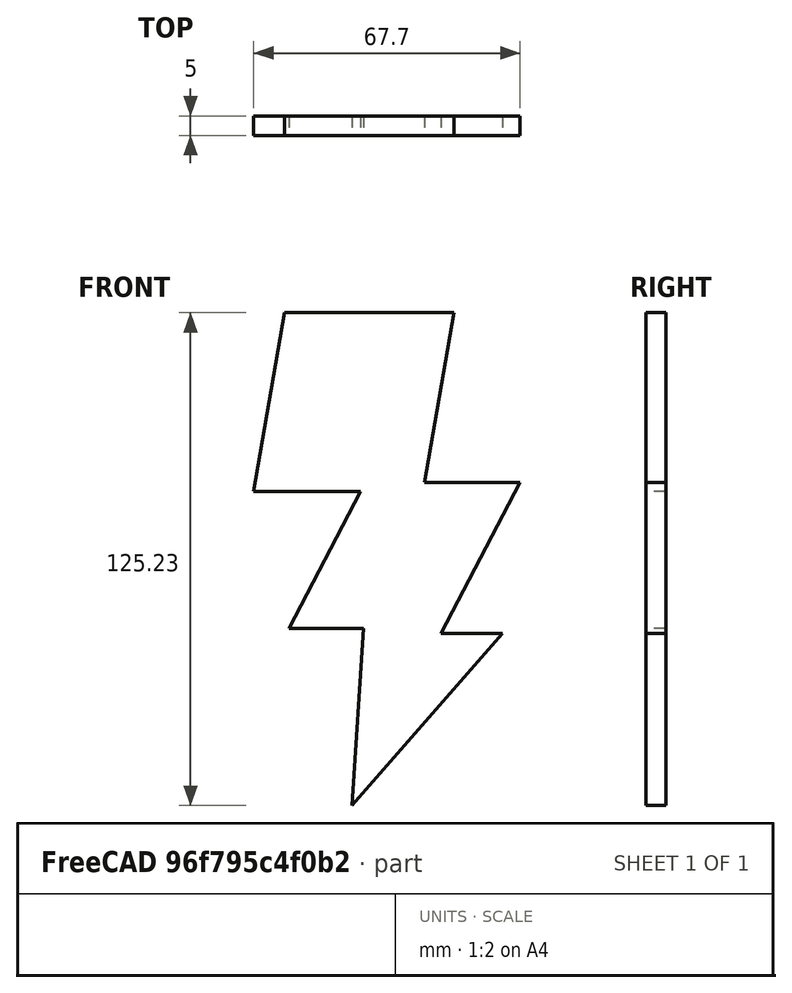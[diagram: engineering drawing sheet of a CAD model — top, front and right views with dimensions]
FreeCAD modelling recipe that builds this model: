
FCSTD DOCUMENT  (FreeCAD 0.18R16146 (Git))
Label: rayo
License: All rights reserved
LicenseURL: http://en.wikipedia.org/wiki/All_rights_reserved
objects: Sketcher::SketchObject×1, PartDesign::Pad×1, PartDesign::Body×1
note: 4 computed .brp shape members not serialized (recipe doc carries the construction recipe); baked Part::Feature solids carry a one-line shape summary decoded from their .brp

FEATURE [Sketcher::SketchObject] Sketch
  MapMode = 5
  Placement = pos=(0,0,0) rot=(1,0,0;1.5708rad)
  Support = -> [XZ_Plane]
  sketch-geometry (11):
    g0: LineSegment StartX=16.8096 StartY=52.0515 StartZ=0 EndX=59.8494 EndY=52.0515 EndZ=0
    g1: LineSegment StartX=59.8494 StartY=52.0515 StartZ=0 EndX=52.4519 EndY=8.97812 EndZ=0
    g2: LineSegment StartX=52.4519 StartY=8.97812 StartZ=0 EndX=76.7074 EndY=8.97812 EndZ=0
    g3: LineSegment StartX=76.7074 StartY=8.97812 StartZ=0 EndX=56.5991 EndY=-29.4804 EndZ=0
    g4: LineSegment StartX=56.5991 StartY=-29.4804 StartZ=0 EndX=72.2487 EndY=-29.4804 EndZ=0
    g5: LineSegment StartX=72.2487 StartY=-29.4804 StartZ=0 EndX=34.0234 EndY=-73.1768 EndZ=0
    g6: LineSegment StartX=34.0234 StartY=-73.1768 StartZ=0 EndX=36.9265 EndY=-28.1238 EndZ=0
    g7: LineSegment StartX=36.9265 StartY=-28.1238 StartZ=0 EndX=17.9519 EndY=-28.1238 EndZ=0
    g8: LineSegment StartX=17.9519 StartY=-28.1238 StartZ=0 EndX=36.135 EndY=6.65246 EndZ=0
    g9: LineSegment StartX=36.135 StartY=6.65246 StartZ=0 EndX=9.01269 EndY=6.65246 EndZ=0
    g10: LineSegment StartX=9.01269 StartY=6.65246 StartZ=0 EndX=16.8096 EndY=52.0515 EndZ=0
  constraints (18):
    c: Horizontal(g0)
    c: Coincident(g0,g1)
    c: Coincident(g1,g2)
    c: Horizontal(g2)
    c: Coincident(g2,g3)
    c: Coincident(g3,g4)
    c: Horizontal(g4)
    c: Coincident(g4,g5)
    c: Coincident(g5,g6)
    c: Coincident(g6,g7)
    c: Horizontal(g7)
    c: Coincident(g7,g8)
    c: Coincident(g8,g9)
    c: Horizontal(g9)
    c: Coincident(g9,g10)
    c: Coincident(g10,g0)
    c: Parallel(g10,g1)
    c: Parallel(g8,g3)
FEATURE [PartDesign::Pad] Pad
  Length = 5
  Length2 = 100
  Placement = pos=(0,0,0) rot=(1,0,0;1.5708rad)
  Profile = -> Sketch
  Refine = true
  Type = 0
FEATURE [PartDesign::Body] Body
  Group = -> [Sketch,Pad]
  Origin = -> Origin
  Tip = -> Pad
